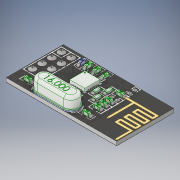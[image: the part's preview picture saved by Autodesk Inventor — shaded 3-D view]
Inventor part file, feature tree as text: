
AUTODESK INVENTOR PART (.ipt)
format: ipt  version: 2019.4 (Build 234330000, 330)  size: 6,771,200 bytes
history: mixed  units: mm
features: other x95, loft x29, boolean_combine x2, imported_body x1
ambient origin geometry x8: Origin, YZ Plane, XZ Plane, XY Plane, X Axis, Y Axis, Z Axis, Center Point
bodies: Solid1 (imported_parasolid), Solid2 (imported_parasolid), Solid3 (imported_parasolid), Solid4 (imported_parasolid), Solid5 (imported_parasolid), Solid6 (imported_parasolid), Solid7 (imported_parasolid), Solid8 (imported_parasolid), Solid9 (imported_parasolid), Solid10 (imported_parasolid), Solid11 (imported_parasolid), Solid12 (imported_parasolid), Solid13 (imported_parasolid), Solid14 (imported_parasolid), Solid15 (imported_parasolid), Solid16 (imported_parasolid), Solid17 (imported_parasolid), Solid18 (imported_parasolid), Solid19 (imported_parasolid), Solid20 (imported_parasolid), Solid21 (imported_parasolid), Solid22 (imported_parasolid), Solid23 (imported_parasolid), Solid24 (imported_parasolid), Solid25 (imported_parasolid), Solid26 (imported_parasolid), Solid27 (imported_parasolid), Solid28 (imported_parasolid), Solid29 (imported_parasolid), Solid30 (imported_parasolid), Solid31 (imported_parasolid), Solid32 (imported_parasolid), Solid33 (imported_parasolid), Solid34 (imported_parasolid), Solid35 (imported_parasolid), Solid36 (imported_parasolid), Solid37 (imported_parasolid), Solid38 (imported_parasolid), Solid39 (imported_parasolid), Solid40 (imported_parasolid), Solid41 (imported_parasolid), Solid42 (imported_parasolid), Solid43 (imported_parasolid), Solid44 (imported_parasolid), Solid45 (imported_parasolid), Solid46 (imported_parasolid), Solid47 (imported_parasolid), Solid48 (imported_parasolid), Solid49 (imported_parasolid), Solid50 (imported_parasolid), Solid51 (imported_parasolid), Solid52 (imported_parasolid), Solid53 (imported_parasolid), Solid54 (imported_parasolid), Solid55 (imported_parasolid), Solid56 (imported_parasolid), Solid57 (imported_parasolid), Solid58 (imported_parasolid), Solid59 (imported_parasolid), Solid60 (imported_parasolid), Solid61 (imported_parasolid), Solid62 (imported_parasolid), Solid63 (imported_parasolid), Solid64 (imported_parasolid), Solid65 (imported_parasolid), Solid66 (imported_parasolid), Solid67 (imported_parasolid), Solid68 (imported_parasolid), Solid69 (imported_parasolid), Solid70 (imported_parasolid), Solid71 (imported_parasolid), Solid72 (imported_parasolid), Solid73 (imported_parasolid), Solid74 (imported_parasolid), Solid75 (imported_parasolid), Solid76 (imported_parasolid), Solid77 (imported_parasolid), Solid78 (imported_parasolid), Solid79 (imported_parasolid), Solid80 (imported_parasolid), Solid81 (imported_parasolid), Solid82 (imported_parasolid), Solid83 (imported_parasolid), Solid84 (imported_parasolid), Solid85 (imported_parasolid), Solid86 (imported_parasolid), Solid87 (imported_parasolid), Solid88 (imported_parasolid), Solid89 (imported_parasolid), Solid90 (imported_parasolid), Solid91 (imported_parasolid), Solid93 (imported_parasolid), Solid94 (imported_parasolid), Solid95 (imported_parasolid), Solid96 (imported_parasolid), Solid97 (imported_parasolid), Solid98 (imported_parasolid), Solid99 (imported_parasolid), Solid100 (imported_parasolid), Solid101 (imported_parasolid), Solid102 (imported_parasolid), Solid103 (imported_parasolid), Solid104 (imported_parasolid), Solid105 (imported_parasolid), Solid106 (imported_parasolid), Solid107 (imported_parasolid), Solid108 (imported_parasolid), Solid109 (imported_parasolid), Solid110 (imported_parasolid), Solid111 (imported_parasolid), Solid112 (imported_parasolid), Solid113 (imported_parasolid), Solid114 (imported_parasolid), Solid115 (imported_parasolid), Solid116 (imported_parasolid), Solid117 (imported_parasolid), Solid118 (imported_parasolid), Solid119 (imported_parasolid), Solid120 (imported_parasolid), Solid121 (imported_parasolid), Solid122 (imported_parasolid), Solid123 (imported_parasolid), Solid124 (imported_parasolid), Solid125 (imported_parasolid), Solid126 (imported_parasolid), Solid127 (imported_parasolid)
feature tree (127):
  other  "PCB Body"
  other  "Cut-Extrude1[2]"
  other  "Cut-Extrude1[3]"
  other  "Cut-Extrude1[4]"
  other  "Cut-Extrude1[5]"
  other  "Cut-Extrude1[6]"
  other  "Cut-Extrude1[7]"
  other  "Cut-Extrude1[8]"
  other  "Cut-Extrude1[9]"
  other  "Cut-Extrude1[10]"
  other  "Cut-Extrude1[11]"
  other  "Cut-Extrude1[12]"
  other  "Cut-Extrude1[13]"
  other  "Cut-Extrude2[1]"
  other  "Cut-Extrude2[2]"
  other  "Cut-Extrude2[3]"
  other  "Cut-Extrude2[4]"
  other  "_Capacitor 1608_-_Solid7_"
  other  "Body-Move_Copy21"
  other  "Body-Move_Copy22"
  other  "_Resistor 1608_-_Imported1_"
  other  "Body-Move_Copy26"
  other  "Body-Move_Copy28"
  other  "Body-Move_Copy29[1]"
  other  "Body-Move_Copy29[2]"
  other  "Body-Move_Copy30"
  other  "Body-Move_Copy31"
  other  "Body-Move_Copy34"
  other  "_rg1608p-103-b_-_rg1608p-103-b_"
  other  "Body-Move_Copy38"
  other  "Body-Move_Copy39"
  other  "_QFN-20 with Pad_-_Вытянуть4_"
  other  "Boss-Extrude22"
  other  "Boss-Extrude28"
  other  "Body-Move_Copy50"
  other  "Boss-Extrude31"
  other  "Cut-Extrude3"
  loft  "Loft2"
  loft  "Loft4"
  loft  "Loft7"
  loft  "Loft9"
  loft  "Loft10"
  loft  "Loft12"
  loft  "Loft13"
  loft  "Loft14"
  loft  "Loft15"
  loft  "Loft16"
  loft  "Loft17"
  loft  "Loft18"
  loft  "Loft19"
  loft  "Loft20"
  loft  "Loft21"
  loft  "Loft22"
  loft  "Loft23"
  loft  "Loft24"
  loft  "Loft25"
  loft  "Loft26"
  loft  "Loft27"
  loft  "Loft28"
  loft  "Loft29"
  loft  "Loft30"
  loft  "Loft31"
  loft  "Loft32"
  loft  "Loft33"
  loft  "Loft34"
  loft  "Loft35"
  other  "Body-Move_Copy51[1]"
  other  "Body-Move_Copy51[2]"
  other  "Body-Move_Copy51[3]"
  other  "Body-Move_Copy51[4]"
  other  "Body-Move_Copy53[1]"
  other  "Body-Move_Copy53[2]"
  other  "Body-Move_Copy53[3]"
  other  "Body-Move_Copy53[4]"
  other  "Body-Move_Copy53[5]"
  other  "Body-Move_Copy57[1]"
  other  "Body-Move_Copy57[2]"
  other  "Body-Move_Copy57[3]"
  other  "Body-Move_Copy57[4]"
  other  "Body-Move_Copy57[5]"
  other  "Body-Move_Copy57[6]"
  other  "Body-Move_Copy57[7]"
  other  "Body-Move_Copy57[8]"
  other  "Body-Move_Copy57[9]"
  other  "Body-Move_Copy57[10]"
  other  "Boss-Extrude38[1]"
  other  "Boss-Extrude38[2]"
  other  "Boss-Extrude38[3]"
  other  "Boss-Extrude38[4]"
  other  "Cut-Extrude4[1]"
  other  "Cut-Extrude4[2]"
  other  "Cut-Extrude5[1]"
  other  "Cut-Extrude5[2]"
  other  "Cut-Extrude5[3]"
  other  "Cut-Extrude5[4]"
  other  "Cut-Extrude5[5]"
  other  "Cut-Extrude5[6]"
  other  "Cut-Extrude5[7]"
  other  "Cut-Extrude5[8]"
  other  "Boss-Extrude43"
  other  "Boss-Extrude45[1]"
  other  "Boss-Extrude45[2]"
  other  "Boss-Extrude45[3]"
  other  "Boss-Extrude45[4]"
  other  "Boss-Extrude45[5]"
  other  "Boss-Extrude45[6]"
  other  "Boss-Extrude45[7]"
  other  "Boss-Extrude45[8]"
  other  "Boss-Extrude45[9]"
  other  "Boss-Extrude45[10]"
  other  "Boss-Extrude45[11]"
  other  "Boss-Extrude45[12]"
  other  "Boss-Extrude45[13]"
  other  "Boss-Extrude45[14]"
  other  "Boss-Extrude45[15]"
  other  "Boss-Extrude45[16]"
  other  "Boss-Extrude45[17]"
  other  "Boss-Extrude45[18]"
  other  "Boss-Extrude45[19]"
  other  "Boss-Extrude45[20]"
  other  "Boss-Extrude45[21]"
  other  "Boss-Extrude45[22]"
  other  "Boss-Extrude45[23]"
  other  "Boss-Extrude45[24]"
  boolean_combine  "Combine15"
  boolean_combine  "Combine16"
  imported_body  NMx_Import_Brep_tag  [imported B-rep: ~522 faces, bbox_mm=None]
